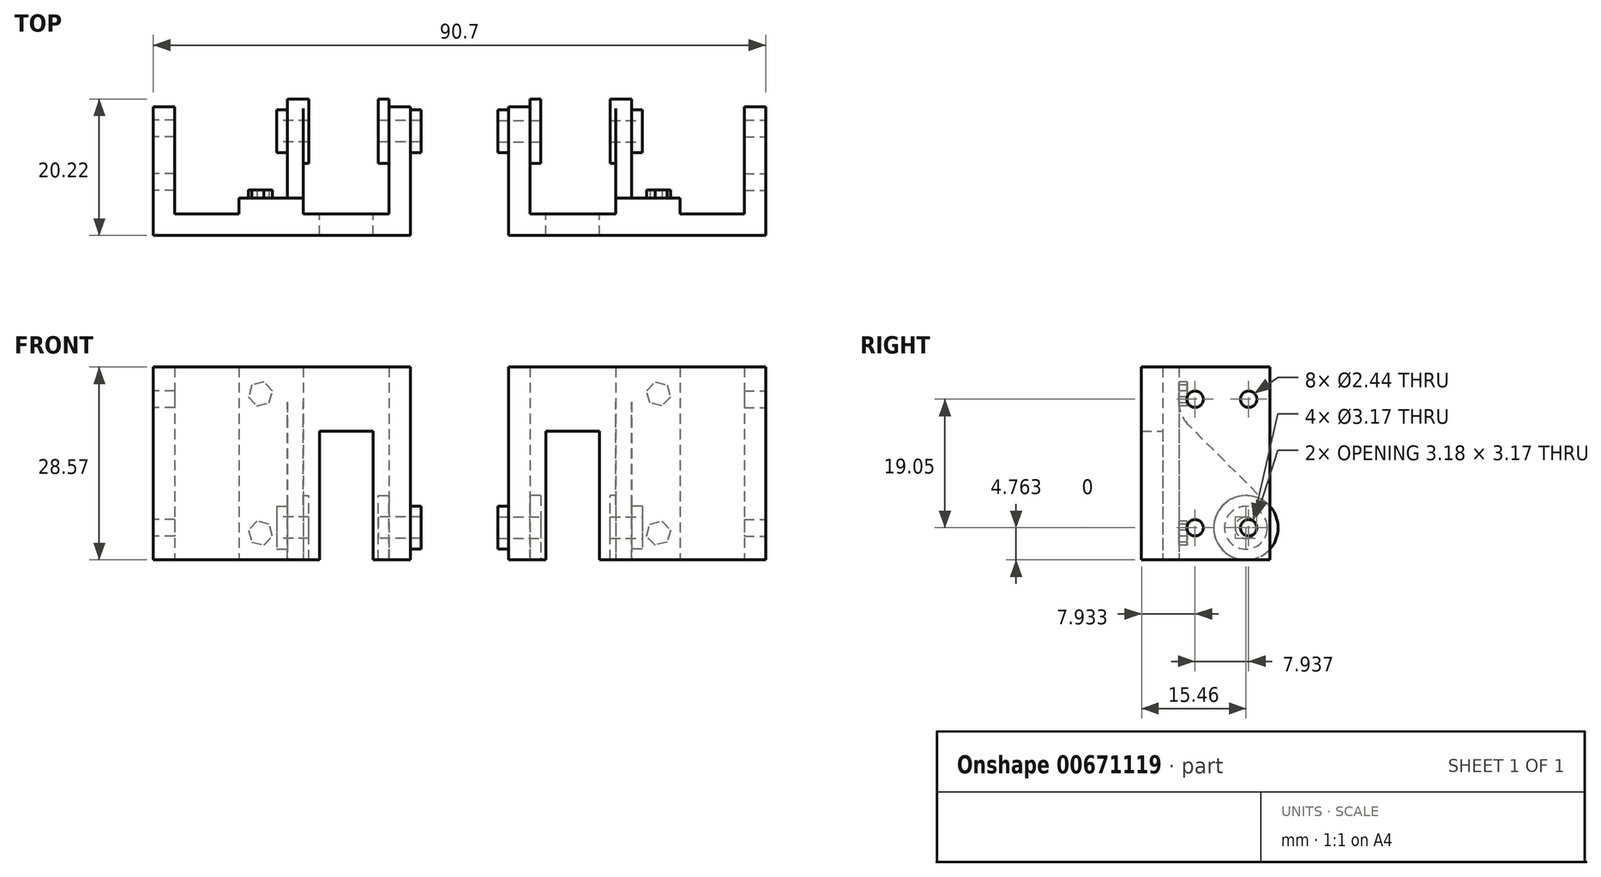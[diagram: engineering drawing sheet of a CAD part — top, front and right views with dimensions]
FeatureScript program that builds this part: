
annotation { "Feature Type Name" : "Feature", "Feature Type Description" : "" }
export const myFeature = defineFeature(function(context is Context, id is Id, definition is map)
    precondition{}
    {
        {
            var Q0;
            Q0=qCreatedBy(makeId("Front.planeOp"),FACE);
            var sketch = newSketch(context, id + "F0", { "sketchPlane" : qUnion([Q0])});
            skLineSegment(sketch, "E0", {"start": v(-7.25, 0) * mm, "end": v(-12.81, 0) * mm});
            skLineSegment(sketch, "E1", {"start": v(-12.81, 0) * mm, "end": v(-12.81, 19.05) * mm});
            skLineSegment(sketch, "E2", {"start": v(-12.81, 19.05) * mm, "end": v(-20.75, 19.05) * mm});
            skLineSegment(sketch, "E3", {"start": v(-20.75, 19.05) * mm, "end": v(-20.75, 0) * mm});
            skLineSegment(sketch, "E4", {"start": v(-20.75, 0) * mm, "end": v(-45.35, 0) * mm});
            skLineSegment(sketch, "E5", {"start": v(-45.35, 0) * mm, "end": v(-45.35, 28.58) * mm});
            skLineSegment(sketch, "E6", {"start": v(-45.35, 28.58) * mm, "end": v(-7.25, 28.58) * mm});
            skLineSegment(sketch, "E7", {"start": v(-7.25, 28.58) * mm, "end": v(-7.25, 0) * mm});
            skSolve(sketch);
        }
        {
            var Q0;
            Q0=qSketchRegion(id+"F0",true);
            extrude(context, id + "F1", {"entities" : qUnion([Q0]), "depth" : 3.17 * mm});
        }
        {
            var Q0;
            Q0=makeQuery(id+"F1.opExtrude","CAP_FACE",FACE,{"disambiguationData":[OSD([sQuery(id+"F0.wireOp",EDGE,"E0"),sQuery(id+"F0.wireOp",EDGE,"E1"),sQuery(id+"F0.wireOp",EDGE,"E2"),sQuery(id+"F0.wireOp",EDGE,"E3"),sQuery(id+"F0.wireOp",EDGE,"E4"),sQuery(id+"F0.wireOp",EDGE,"E5"),sQuery(id+"F0.wireOp",EDGE,"E6"),sQuery(id+"F0.wireOp",EDGE,"E7")])],"isStart":true});
            var sketch = newSketch(context, id + "F2", { "sketchPlane" : qUnion([Q0])});
            skLineSegment(sketch, "E8", {"start": v(10.43, 28.58) * mm, "end": v(10.43, 0) * mm});
            skLineSegment(sketch, "E9", {"start": v(42.18, 28.58) * mm, "end": v(42.18, 0) * mm});
            skSolve(sketch);
        }
        {
            var Q0;
            {var subQ0=sQuery(id+"F2.wireOp",EDGE,"E9");Q0=makeQuery(id+"F2.imprint","IMPRINT",FACE,{"disambiguationData":[TD([[makeQuery(id+"F2.imprint","IMPRINT",EDGE,{"derivedFrom":subQ0}),1.0]])]});}
            extrude(context, id + "F3", {"entities" : qUnion([Q0]), "operationType" : NewBodyOperationType.ADD, "depth" : 15.88 * mm});
        }
        {
            var Q0;
            Q0=makeQuery(id+"F1.opExtrude","CAP_FACE",FACE,{"disambiguationData":[OSD([sQuery(id+"F0.wireOp",EDGE,"E0"),sQuery(id+"F0.wireOp",EDGE,"E1"),sQuery(id+"F0.wireOp",EDGE,"E2"),sQuery(id+"F0.wireOp",EDGE,"E3"),sQuery(id+"F0.wireOp",EDGE,"E4"),sQuery(id+"F0.wireOp",EDGE,"E5"),sQuery(id+"F0.wireOp",EDGE,"E6"),sQuery(id+"F0.wireOp",EDGE,"E7")])],"isStart":true});
            var sketch = newSketch(context, id + "F4", { "sketchPlane" : qUnion([Q0])});
            skLineSegment(sketch, "E10", {"start": v(10.43, 28.58) * mm, "end": v(10.43, 0) * mm});
            skSolve(sketch);
        }
        {
            var Q0;
            Q0=qSketchRegion(id+"F4",true);
            var Q1;
            {var subQ0=sQuery(id+"F4.wireOp",EDGE,"E10");Q1=makeQuery(id+"F4.imprint","IMPRINT",FACE,{"disambiguationData":[TD([[makeQuery(id+"F4.imprint","IMPRINT",EDGE,{"derivedFrom":subQ0}),-1.0]])]});}
            extrude(context, id + "F5", {"entities" : qUnion([Q0, Q1]), "operationType" : NewBodyOperationType.ADD, "depth" : 15.88 * mm});
        }
        {
            var Q0;
            Q0=makeQuery(id+"F1.opExtrude","CAP_FACE",FACE,{"disambiguationData":[OSD([sQuery(id+"F0.wireOp",EDGE,"E0"),sQuery(id+"F0.wireOp",EDGE,"E1"),sQuery(id+"F0.wireOp",EDGE,"E2"),sQuery(id+"F0.wireOp",EDGE,"E3"),sQuery(id+"F0.wireOp",EDGE,"E4"),sQuery(id+"F0.wireOp",EDGE,"E5"),sQuery(id+"F0.wireOp",EDGE,"E6"),sQuery(id+"F0.wireOp",EDGE,"E7")])],"isStart":true});
            var sketch = newSketch(context, id + "F6", { "sketchPlane" : qUnion([Q0])});
            skLineSegment(sketch, "E11", {"start": v(23.13, 28.58) * mm, "end": v(23.13, 0) * mm});
            skLineSegment(sketch, "E12", {"start": v(32.65, 28.58) * mm, "end": v(32.65, 0) * mm});
            skSolve(sketch);
        }
        {
            var Q0;
            {var subQ0=sQuery(id+"F6.wireOp",EDGE,"E11");Q0=makeQuery(id+"F6.imprint","IMPRINT",FACE,{"disambiguationData":[TD([[makeQuery(id+"F6.imprint","IMPRINT",EDGE,{"derivedFrom":subQ0}),1.0]])]});}
            extrude(context, id + "F7", {"entities" : qUnion([Q0]), "operationType" : NewBodyOperationType.ADD, "depth" : 2.38 * mm});
        }
        {
            var Q0;
            Q0=makeQuery(id+"F7.opExtrude","CAP_FACE",FACE,{"disambiguationData":[OSD([sQuery(id+"F0.wireOp",EDGE,"E4"),sQuery(id+"F0.wireOp",EDGE,"E6"),sQuery(id+"F6.wireOp",EDGE,"E11"),sQuery(id+"F6.wireOp",EDGE,"E12")])],"isStart":false});
            var sketch = newSketch(context, id + "F8", { "sketchPlane" : qUnion([Q0])});
            skLineSegment(sketch, "E13", {"start": v(25.51, 28.58) * mm, "end": v(25.51, 0) * mm});
            skSolve(sketch);
        }
        {
            var Q0;
            Q0=qSketchRegion(id+"F8",true);
            var Q1;
            {var subQ0=sQuery(id+"F8.wireOp",EDGE,"E13");Q1=makeQuery(id+"F8.imprint","IMPRINT",FACE,{"disambiguationData":[TD([[makeQuery(id+"F8.imprint","IMPRINT",EDGE,{"derivedFrom":subQ0}),-1.0]])]});}
            extrude(context, id + "F9", {"entities" : qUnion([Q0, Q1]), "operationType" : NewBodyOperationType.ADD, "depth" : 15.08 * mm});
        }
        {
            var Q0;
            {var subQ0=sQuery(id+"F6.wireOp",EDGE,"E11");Q0=makeQuery(id+"F9.boolean.opBoolean","MERGE",FACE,{"derivedFrom":[makeQuery(id+"F7.opExtrude","SWEPT_FACE",FACE,{"disambiguationData":[OSD([subQ0])]}),makeQuery(id+"F9.opExtrude","SWEPT_FACE",FACE,{"disambiguationData":[OSD([subQ0])]})]});}
            var sketch = newSketch(context, id + "F10", { "sketchPlane" : qUnion([Q0])});
            skCircle(sketch, "E14", {"center": v(12.3, 4.76) * mm, "radius": 4.76 * mm});
            skLineSegment(sketch, "E15", {"start": v(2.38, 28.58) * mm, "end": v(2.38, 11.63) * mm});
            skLineSegment(sketch, "E16", {"start": v(15.66, 8.13) * mm, "end": v(2.38, 21.4) * mm});
            skSolve(sketch);
        }
        {
            var Q0;
            {var subQ5=sQuery(id+"F10.wireOp",EDGE,"E16");Q0=makeQuery(id+"F10.imprint","IMPRINT",FACE,{"disambiguationData":[TD([[makeQuery(id+"F10.imprint","IMPRINT",EDGE,{"derivedFrom":subQ5}),-1.0]])]});}
            extrude(context, id + "F11", {"entities" : qUnion([Q0]), "operationType" : NewBodyOperationType.REMOVE, "oppositeDirection" : true, "depth" : 2.38 * mm});
        }
        {
            var Q0;
            Q0=makeQuery(id+"F11.boolean.opBoolean","COPY",EDGE,{"derivedFrom":makeQuery(id+"F11.opExtrude","SWEPT_EDGE",EDGE,{"disambiguationData":[OSD([sQuery(id+"F10.wireOp",EDGE,"E15"),sQuery(id+"F10.wireOp",EDGE,"E16")])]})});
            fillet(context, id + "F12", {"entities" : qUnion([Q0]), "radius" : 4.76 * mm, "tangentPropagation" : true, "allowEdgeOverflow" : false});
        }
        {
            var Q0;
            {var subQ0=sQuery(id+"F6.wireOp",EDGE,"E11");Q0=makeQuery(id+"F9.boolean.opBoolean","MERGE",FACE,{"derivedFrom":[makeQuery(id+"F7.opExtrude","SWEPT_FACE",FACE,{"disambiguationData":[OSD([subQ0])]}),makeQuery(id+"F9.opExtrude","SWEPT_FACE",FACE,{"disambiguationData":[OSD([subQ0])]})]});}
            var sketch = newSketch(context, id + "F13", { "sketchPlane" : qUnion([Q0])});
            skCircle(sketch, "E17", {"center": v(12.3, 4.76) * mm, "radius": 4.76 * mm});
            skSolve(sketch);
        }
        {
            var Q0;
            Q0=qSketchRegion(id+"F13",true);
            extrude(context, id + "F14", {"entities" : qUnion([Q0]), "operationType" : NewBodyOperationType.ADD, "depth" : 0.8 * mm});
        }
        {
            var Q0;
            Q0=makeQuery(id+"F9.opExtrude","SWEPT_FACE",FACE,{"disambiguationData":[OSD([sQuery(id+"F8.wireOp",EDGE,"E13")])]});
            var sketch = newSketch(context, id + "F15", { "sketchPlane" : qUnion([Q0])});
            skCircle(sketch, "E18", {"center": v(-12.3, 4.76) * mm, "radius": 3.17 * mm});
            skSolve(sketch);
        }
        {
            var Q0;
            Q0=qSketchRegion(id+"F15",true);
            extrude(context, id + "F16", {"entities" : qUnion([Q0]), "operationType" : NewBodyOperationType.ADD, "depth" : 1.59 * mm});
        }
        {
            var Q0;
            Q0=makeQuery(id+"F16.opExtrude","CAP_FACE",FACE,{"disambiguationData":[OSD([sQuery(id+"F15.wireOp",EDGE,"E18")])],"isStart":false});
            var sketch = newSketch(context, id + "F17", { "sketchPlane" : qUnion([Q0])});
            skCircle(sketch, "E19", {"center": v(-12.3, 4.76) * mm, "radius": 1.59 * mm});
            skSolve(sketch);
        }
        {
            var Q0;
            Q0=qSketchRegion(id+"F17",true);
            extrude(context, id + "F18", {"entities" : qUnion([Q0]), "operationType" : NewBodyOperationType.REMOVE, "oppositeDirection" : true, "depth" : 25.4 * mm});
        }
        {
            var Q0;
            Q0=makeQuery(id+"F5.opExtrude","SWEPT_FACE",FACE,{"disambiguationData":[OSD([sQuery(id+"F4.wireOp",EDGE,"E10")])]});
            var sketch = newSketch(context, id + "F19", { "sketchPlane" : qUnion([Q0])});
            skCircle(sketch, "E20", {"center": v(-12.3, 4.76) * mm, "radius": 4.76 * mm});
            skSolve(sketch);
        }
        {
            var Q0;
            {var subQ1=sQuery(id+"F4.wireOp",EDGE,"E10");Q0=makeQuery(id+"F19.imprint","IMPRINT",FACE,{"disambiguationData":[TD([[makeQuery(id+"F19.imprint","IMPRINT",EDGE,{"derivedFrom":makeQuery(id+"F18.boolean.opBoolean","INTERSECT",EDGE,{"derivedFrom":[makeQuery(id+"F5.opExtrude","SWEPT_FACE",FACE,{"disambiguationData":[OSD([subQ1])]}),makeQuery(id+"F18.opExtrude","SWEPT_FACE",FACE,{"disambiguationData":[OSD([sQuery(id+"F17.wireOp",EDGE,"E19")])]})]})}),-1.0]])]});}
            var Q1;
            {var subQ0=sQuery(id+"F19.wireOp",EDGE,"E20");var subQ1=makeQuery(id+"F5.opExtrude","CAP_EDGE",EDGE,{"disambiguationData":[OSD([sQuery(id+"F4.wireOp",EDGE,"E10")])],"isStart":false});var subQ2=makeQuery(id+"F19.imprint","INTERSECT",VERTEX,{"disambiguationData":[OD(0.0)],"derivedFrom":[subQ1,subQ0]});Q1=makeQuery(id+"F19.imprint","IMPRINT",FACE,{"disambiguationData":[TD([[makeQuery(id+"F19.imprint","IMPRINT",EDGE,{"disambiguationData":[TD([[subQ2,1.0]])],"derivedFrom":subQ0}),1.0]])]});}
            extrude(context, id + "F20", {"entities" : qUnion([Q0, Q1]), "operationType" : NewBodyOperationType.ADD, "depth" : 1.59 * mm});
        }
        {
            var Q0;
            {var subQ0=sQuery(id+"F0.wireOp",EDGE,"E7");Q0=makeQuery(id+"F5.boolean.opBoolean","MERGE",FACE,{"derivedFrom":[makeQuery(id+"F1.opExtrude","SWEPT_FACE",FACE,{"disambiguationData":[OSD([subQ0])]}),makeQuery(id+"F5.opExtrude","SWEPT_FACE",FACE,{"disambiguationData":[OSD([subQ0])]})]});}
            var sketch = newSketch(context, id + "F21", { "sketchPlane" : qUnion([Q0])});
            skCircle(sketch, "E21", {"center": v(12.3, 4.76) * mm, "radius": 3.18 * mm});
            skSolve(sketch);
        }
        {
            var Q0;
            Q0=makeQuery(id+"F21.imprint","IMPRINT",FACE,{"disambiguationData":[TD([[makeQuery(id+"F21.imprint","IMPRINT",EDGE,{"derivedFrom":sQuery(id+"F21.wireOp",EDGE,"E21")}),1.0]])]});
            extrude(context, id + "F22", {"entities" : qUnion([Q0]), "operationType" : NewBodyOperationType.ADD, "depth" : 1.59 * mm});
        }
        {
            var Q0;
            {var subQ0=sQuery(id+"F0.wireOp",EDGE,"E5");Q0=makeQuery(id+"F3.boolean.opBoolean","MERGE",FACE,{"derivedFrom":[makeQuery(id+"F1.opExtrude","SWEPT_FACE",FACE,{"disambiguationData":[OSD([subQ0])]}),makeQuery(id+"F3.opExtrude","SWEPT_FACE",FACE,{"disambiguationData":[OSD([subQ0])]})]});}
            var sketch = newSketch(context, id + "F23", { "sketchPlane" : qUnion([Q0])});
            skCircle(sketch, "E22", {"center": v(-12.7, 23.81) * mm, "radius": 1.22 * mm});
            skCircle(sketch, "E23", {"center": v(-4.76, 23.81) * mm, "radius": 1.22 * mm});
            skCircle(sketch, "E24", {"center": v(-12.7, 4.76) * mm, "radius": 1.22 * mm});
            skCircle(sketch, "E25", {"center": v(-4.76, 4.76) * mm, "radius": 1.22 * mm});
            skSolve(sketch);
        }
        {
            var Q0;
            Q0=qSketchRegion(id+"F23",true);
            extrude(context, id + "F24", {"entities" : qUnion([Q0]), "operationType" : NewBodyOperationType.REMOVE, "oppositeDirection" : true, "depth" : 4.76 * mm});
        }
        {
            var Q0;
            Q0=makeQuery(id+"F11.boolean.opBoolean","MERGE",FACE,{"derivedFrom":[makeQuery(id+"F7.opExtrude","CAP_FACE",FACE,{"disambiguationData":[OSD([sQuery(id+"F0.wireOp",EDGE,"E4"),sQuery(id+"F0.wireOp",EDGE,"E6"),sQuery(id+"F6.wireOp",EDGE,"E11"),sQuery(id+"F6.wireOp",EDGE,"E12")])],"isStart":false}),makeQuery(id+"F11.opExtrude","SWEPT_FACE",FACE,{"disambiguationData":[OSD([sQuery(id+"F10.wireOp",EDGE,"E15")])]})]});
            var sketch = newSketch(context, id + "F25", { "sketchPlane" : qUnion([Q0])});
            skCircle(sketch, "E26.cCircle", {"center": v(29.48, 24.6) * mm, "radius": 1.59 * mm, "construction": true});
            skLineSegment(sketch, "E26.0", {"start": v(31.26, 24.17) * mm, "end": v(30, 22.85) * mm});
            skLineSegment(sketch, "E26.1", {"start": v(30, 22.85) * mm, "end": v(28.21, 23.28) * mm});
            skLineSegment(sketch, "E26.2", {"start": v(28.21, 23.28) * mm, "end": v(27.7, 25.04) * mm});
            skLineSegment(sketch, "E26.3", {"start": v(27.7, 25.04) * mm, "end": v(28.97, 26.37) * mm});
            skLineSegment(sketch, "E26.4", {"start": v(28.97, 26.37) * mm, "end": v(30.75, 25.93) * mm});
            skLineSegment(sketch, "E26.5", {"start": v(30.75, 25.93) * mm, "end": v(31.26, 24.17) * mm});
            skPoint(sketch, "E26.0.midPoint", {"position": v(30.63, 23.5) * mm});
            skCircle(sketch, "E27.cCircle", {"center": v(29.48, 3.97) * mm, "radius": 1.59 * mm, "construction": true});
            skLineSegment(sketch, "E27.0", {"start": v(30.76, 2.65) * mm, "end": v(28.98, 2.2) * mm});
            skLineSegment(sketch, "E27.1", {"start": v(28.98, 2.2) * mm, "end": v(27.7, 3.52) * mm});
            skLineSegment(sketch, "E27.2", {"start": v(27.7, 3.52) * mm, "end": v(28.2, 5.28) * mm});
            skLineSegment(sketch, "E27.3", {"start": v(28.2, 5.28) * mm, "end": v(29.98, 5.73) * mm});
            skLineSegment(sketch, "E27.4", {"start": v(29.98, 5.73) * mm, "end": v(31.26, 4.42) * mm});
            skLineSegment(sketch, "E27.5", {"start": v(31.26, 4.42) * mm, "end": v(30.76, 2.65) * mm});
            skPoint(sketch, "E27.0.midPoint", {"position": v(29.87, 2.43) * mm});
            skSolve(sketch);
        }
        {
            var Q0;
            Q0=qSketchRegion(id+"F25",true);
            extrude(context, id + "F26", {"entities" : qUnion([Q0]), "operationType" : NewBodyOperationType.ADD, "depth" : 1.2 * mm});
        }
        {
            var Q0;
            Q0=makeQuery(id+"F1.opExtrude","SWEPT_BODY",BODY,{"disambiguationData":[OSD([sQuery(id+"F0.wireOp",EDGE,"E0"),sQuery(id+"F0.wireOp",EDGE,"E1"),sQuery(id+"F0.wireOp",EDGE,"E2"),sQuery(id+"F0.wireOp",EDGE,"E3"),sQuery(id+"F0.wireOp",EDGE,"E4"),sQuery(id+"F0.wireOp",EDGE,"E5"),sQuery(id+"F0.wireOp",EDGE,"E6"),sQuery(id+"F0.wireOp",EDGE,"E7")])]});
            var Q1;
            Q1=qCreatedBy(makeId("Right.planeOp"),FACE);
            mirror(context, id + "F27", {"entities" : qUnion([Q0]), "mirrorPlane" : qUnion([Q1])});
        }
    });
